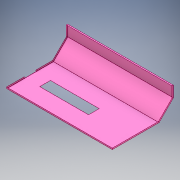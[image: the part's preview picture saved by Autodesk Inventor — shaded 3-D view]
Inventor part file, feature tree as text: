
AUTODESK INVENTOR PART (.ipt)
format: ipt  version: 2018 (Build 220112000, 112)  size: 274,432 bytes
history: native  units: mm
features: sheet_metal_op x13, sketch x7, other x5, extrude x2
ambient origin geometry x8: Origin, YZ Plane, XZ Plane, XY Plane, X Axis, Y Axis, Z Axis, Center Point
bodies: Solid1 (feature_tree)
feature tree (27):
  sheet_metal_op  "Face1"
  sheet_metal_op  "Flange1"
  sheet_metal_op  "Flange2"
  sheet_metal_op  "Flange3"
  extrude  "Extrusion1"  Depth=625.0mm
  sheet_metal_op  "Flange4"
  extrude  "Extrusion2"  Depth=1.6mm
  sketch  "Sketch1"  dims[d0=1410.0mm d1=625.0mm]
  other  "Plate1"
  sketch  "Sketch2"  dims[d2=1.6mm d3=1.6mm]
  other  "Plate2"
  sheet_metal_op  "Bend1"
  sheet_metal_op  "Corner1"
  sketch  "Sketch3"  dims[d4=0.8mm]
  other  "Plate3"
  sheet_metal_op  "Bend2"
  sheet_metal_op  "Corner2"
  sketch  "Sketch4"  dims[d5=3.2mm]
  other  "Plate4"
  sheet_metal_op  "Bend3"
  sheet_metal_op  "Corner3"
  sketch  "Sketch5"  dims[d6=1.6mm]
  sketch  "Sketch6"  dims[d7=270.0mm d8=45.0deg d9=1.6mm]
  other  "Plate5"
  sheet_metal_op  "Bend4"
  sheet_metal_op  "Corner4"
  sketch  "Sketch8"  dims[d10=6.4mm d11=1.6mm d12=1.6mm d13=1.6mm d14=0.8mm d15=3.2mm d16=1.6mm d17=150.0mm d18=45.0deg d19=1.6mm d20=6.4mm d21=1.6mm d22=1.6mm d23=1.6mm d24=0.8mm d25=3.2mm d26=1.6mm d27=20.0mm d28=90.0deg d29=1.6mm d30=6.4mm d31=1.6mm d32=1.6mm d33=650.0mm d34=140.0mm d36=195.0mm d37=10.0mm d38=0.0mm d39=1.6mm d40=0.8mm d41=3.2mm d42=1.6mm d43=75.0mm d44=13.962634mm d45=1.6mm d46=6.4mm d47=1.6mm d48=1.6mm d49=245.0mm d52=20.0mm d53=155.0mm d54=10.0mm d55=0.0mm]
